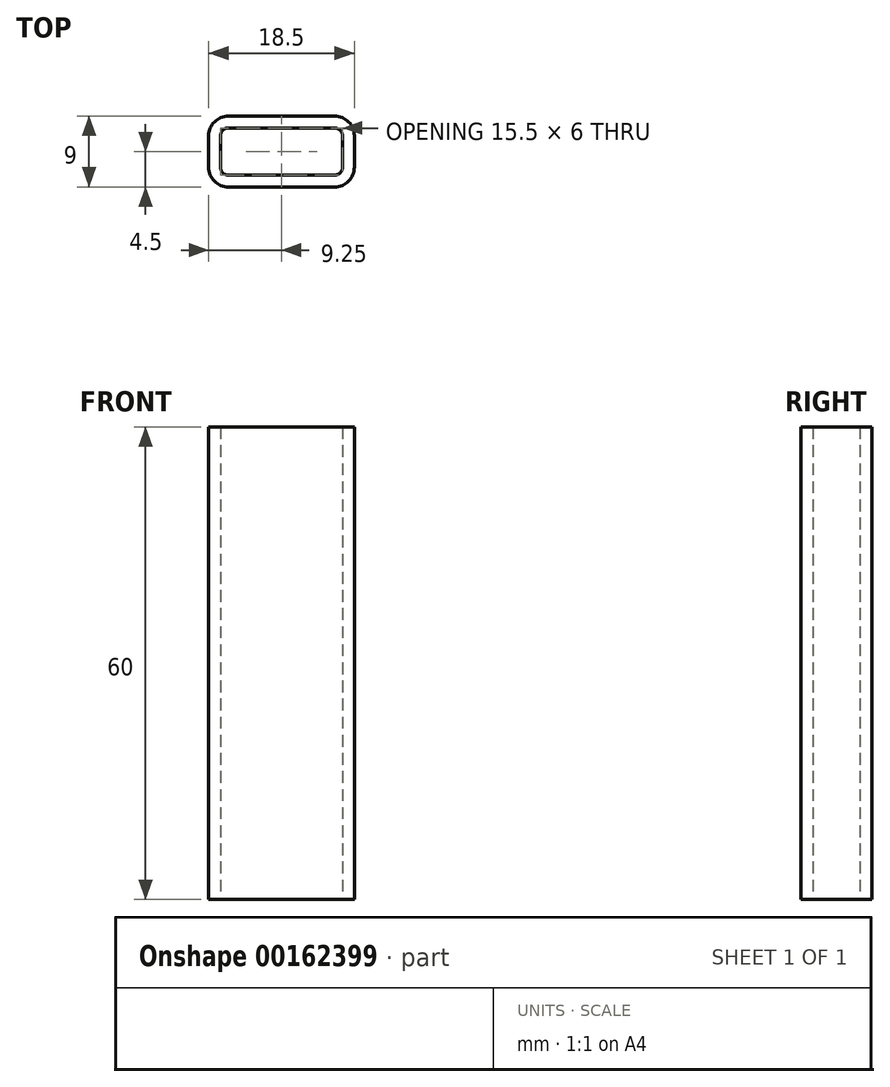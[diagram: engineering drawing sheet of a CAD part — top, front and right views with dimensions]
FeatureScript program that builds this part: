
annotation { "Feature Type Name" : "Feature", "Feature Type Description" : "" }
export const myFeature = defineFeature(function(context is Context, id is Id, definition is map)
    precondition{}
    {
        {
            var Q0;
            Q0=qCreatedBy(makeId("Top.planeOp"),FACE);
            var sketch = newSketch(context, id + "F0", { "sketchPlane" : qUnion([Q0])});
            skArc(sketch, "E0", {"start": v(-6.75, 4.5) * mm, "mid": v(-8.52, 3.77) * mm, "end": v(-9.25, 2) * mm});
            skArc(sketch, "E1", {"start": v(9.25, 2) * mm, "mid": v(8.52, 3.77) * mm, "end": v(6.75, 4.5) * mm});
            skArc(sketch, "E2", {"start": v(6.75, -4.5) * mm, "mid": v(8.52, -3.77) * mm, "end": v(9.25, -2) * mm});
            skArc(sketch, "E3", {"start": v(-9.25, -2) * mm, "mid": v(-8.52, -3.77) * mm, "end": v(-6.75, -4.5) * mm});
            skLineSegment(sketch, "E4", {"start": v(-9.25, 2) * mm, "end": v(-9.25, -2) * mm});
            skLineSegment(sketch, "E5", {"start": v(-6.75, 4.5) * mm, "end": v(6.75, 4.5) * mm});
            skLineSegment(sketch, "E6", {"start": v(9.25, 2) * mm, "end": v(9.25, -2) * mm});
            skLineSegment(sketch, "E7", {"start": v(6.75, -4.5) * mm, "end": v(-6.75, -4.5) * mm});
            skSolve(sketch);
        }
        {
            var Q0;
            Q0 = qSketchRegion(id + "F0", true);
            extrude(context, id + "F1", {"entities" : qUnion([Q0]), "depth" : 60 * mm});
        }
        {
            var Q0;
            Q0=makeQuery(id+"F1.opExtrude","CAP_FACE",FACE,{"disambiguationData":[OSD([sQuery(id+"F0.wireOp",EDGE,"E0"),sQuery(id+"F0.wireOp",EDGE,"E1"),sQuery(id+"F0.wireOp",EDGE,"E2"),sQuery(id+"F0.wireOp",EDGE,"E3"),sQuery(id+"F0.wireOp",EDGE,"E4"),sQuery(id+"F0.wireOp",EDGE,"E5"),sQuery(id+"F0.wireOp",EDGE,"E6"),sQuery(id+"F0.wireOp",EDGE,"E7")])],"isStart":true});
            var sketch = newSketch(context, id + "F2", { "sketchPlane" : qUnion([Q0])});
            skArc(sketch, "E8", {"start": v(-6.75, 3) * mm, "mid": v(-7.46, 2.7) * mm, "end": v(-7.75, 2) * mm});
            skArc(sketch, "E9", {"start": v(7.75, 2) * mm, "mid": v(7.46, 2.7) * mm, "end": v(6.75, 3) * mm});
            skArc(sketch, "E10", {"start": v(6.75, -3) * mm, "mid": v(7.46, -2.7) * mm, "end": v(7.75, -2) * mm});
            skLineSegment(sketch, "E11", {"start": v(-6.75, 3) * mm, "end": v(6.75, 3) * mm});
            skLineSegment(sketch, "E12", {"start": v(7.75, 2) * mm, "end": v(7.75, -2) * mm});
            skLineSegment(sketch, "E13", {"start": v(6.75, -3) * mm, "end": v(-6.75, -3) * mm});
            skLineSegment(sketch, "E14", {"start": v(-7.75, 2) * mm, "end": v(-7.75, -2) * mm});
            skArc(sketch, "E15", {"start": v(-7.75, -2) * mm, "mid": v(-7.46, -2.7) * mm, "end": v(-6.75, -3) * mm});
            skSolve(sketch);
        }
        {
            var Q0;
            Q0 = qSketchRegion(id + "F2", true);
            extrude(context, id + "F3", {"entities" : qUnion([Q0]), "operationType" : NewBodyOperationType.REMOVE, "endBound" : BoundingType.THROUGH_ALL, "oppositeDirection" : true, "depth" : 25 * mm});
        }
    });
